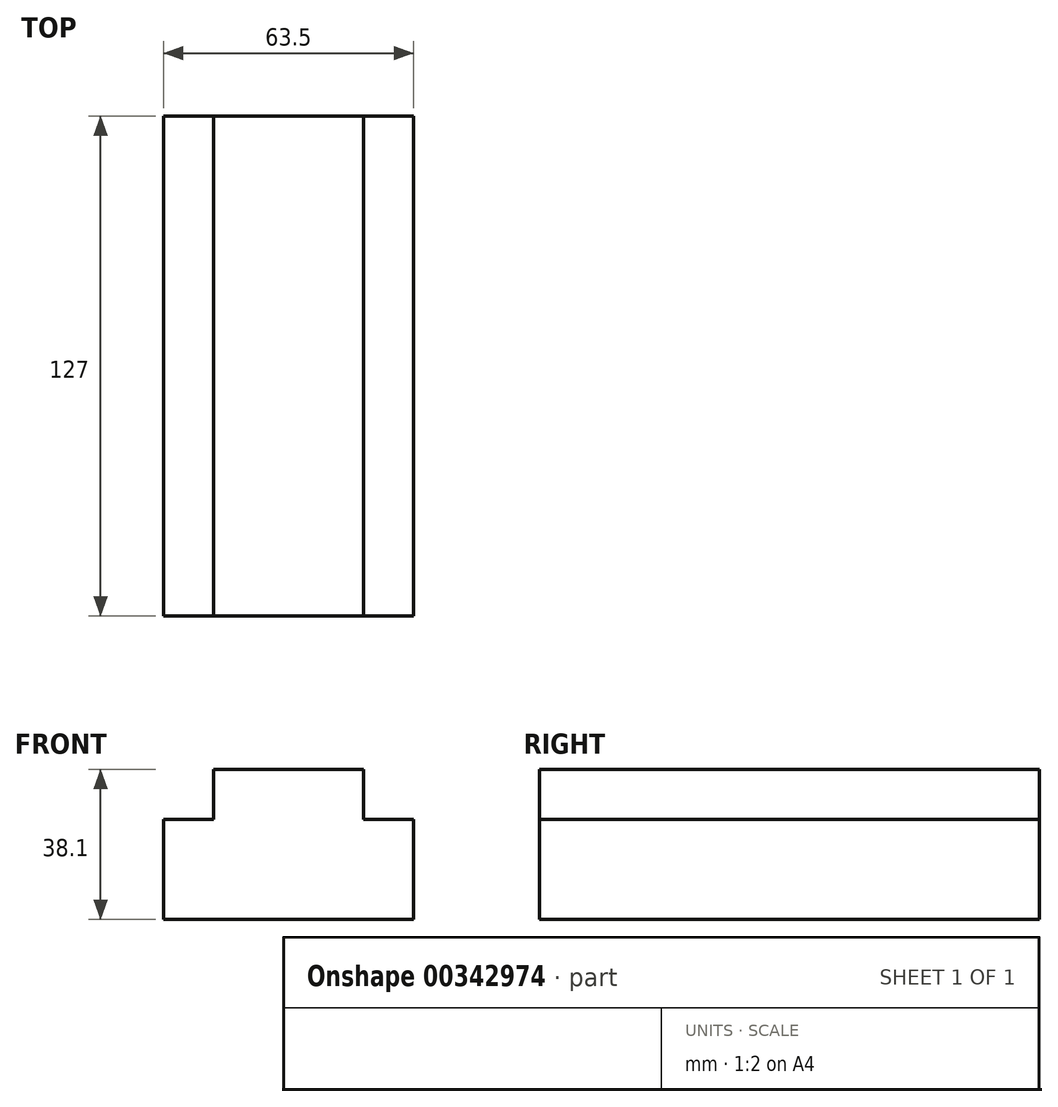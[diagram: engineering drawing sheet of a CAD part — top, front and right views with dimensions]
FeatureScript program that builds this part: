
annotation { "Feature Type Name" : "Feature", "Feature Type Description" : "" }
export const myFeature = defineFeature(function(context is Context, id is Id, definition is map)
    precondition{}
    {
        {
            var Q0;
            Q0=qCreatedBy(makeId("Front.planeOp"),FACE);
            var sketch = newSketch(context, id + "F0", { "sketchPlane" : qUnion([Q0])});
            skLineSegment(sketch, "E0", {"start": v(-30, -41.83) * mm, "end": v(33.5, -41.83) * mm});
            skLineSegment(sketch, "E1", {"start": v(-30, -41.83) * mm, "end": v(-30, -16.43) * mm});
            skLineSegment(sketch, "E2", {"start": v(33.5, -41.83) * mm, "end": v(33.5, -16.43) * mm});
            skLineSegment(sketch, "E3", {"start": v(-30, -16.43) * mm, "end": v(-17.3, -16.43) * mm});
            skLineSegment(sketch, "E4", {"start": v(33.5, -16.43) * mm, "end": v(20.8, -16.43) * mm});
            skLineSegment(sketch, "E5", {"start": v(20.8, -16.43) * mm, "end": v(20.8, -3.73) * mm});
            skLineSegment(sketch, "E6", {"start": v(-17.3, -16.43) * mm, "end": v(-17.3, -3.73) * mm});
            skLineSegment(sketch, "E7", {"start": v(-17.3, -3.73) * mm, "end": v(20.8, -3.73) * mm});
            skSolve(sketch);
        }
        {
            var Q0;
            Q0 = qSketchRegion(id + "F0", true);
            extrude(context, id + "F1", {"entities" : qUnion([Q0]), "depth" : 127 * mm});
        }
    });
